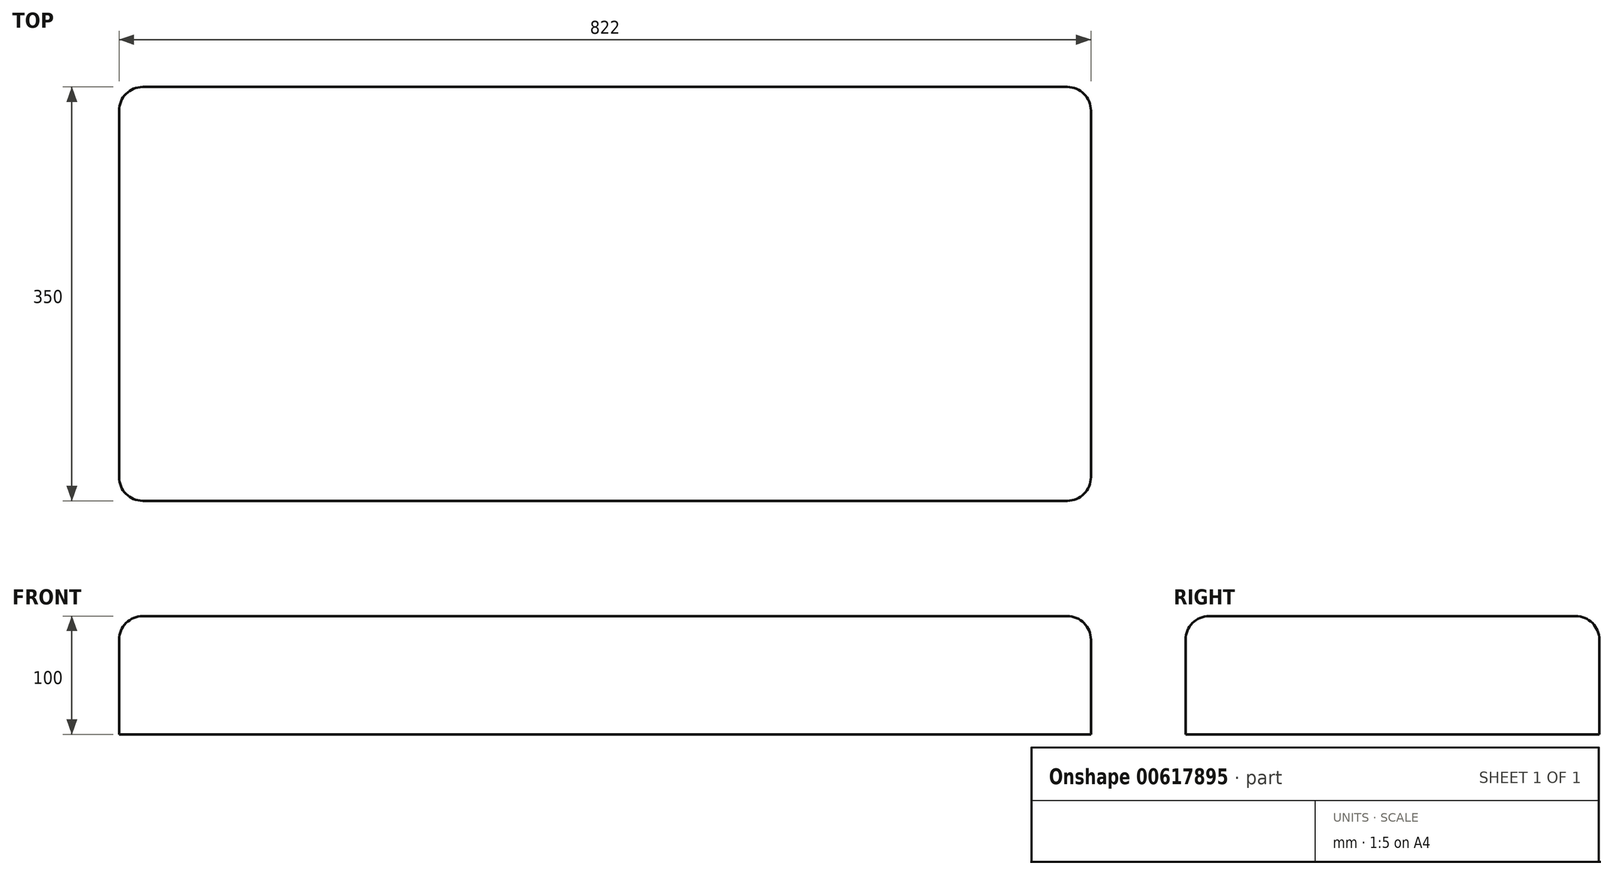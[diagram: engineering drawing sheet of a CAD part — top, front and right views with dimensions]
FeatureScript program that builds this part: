
annotation { "Feature Type Name" : "Feature", "Feature Type Description" : "" }
export const myFeature = defineFeature(function(context is Context, id is Id, definition is map)
    precondition{}
    {
        {
            var Q0;
            Q0=qCreatedBy(makeId("Top.planeOp"),FACE);
            var sketch = newSketch(context, id + "F0", { "sketchPlane" : qUnion([Q0])});
            skLineSegment(sketch, "E0.bottom", {"start": v(411, -175) * mm, "end": v(-411, -175) * mm});
            skLineSegment(sketch, "E0.top", {"start": v(411, 175) * mm, "end": v(-411, 175) * mm});
            skLineSegment(sketch, "E0.left", {"start": v(411, -175) * mm, "end": v(411, 175) * mm});
            skLineSegment(sketch, "E0.right", {"start": v(-411, -175) * mm, "end": v(-411, 175) * mm});
            skPoint(sketch, "E0.middle", {"position": v(0, 0) * mm});
            skSolve(sketch);
        }
        {
            var Q0;
            Q0=qSketchRegion(id+"F0",true);
            extrude(context, id + "F1", {"entities" : qUnion([Q0]), "depth" : 100 * mm, "offsetDistance" : 25 * mm});
        }
        {
            var Q0;
            Q0=makeQuery(id+"F1.opExtrude","CAP_EDGE",EDGE,{"disambiguationData":[OSD([sQuery(id+"F0.wireOp",EDGE,"E0.bottom")])],"isStart":false});
            var Q1;
            Q1=makeQuery(id+"F1.opExtrude","CAP_EDGE",EDGE,{"disambiguationData":[OSD([sQuery(id+"F0.wireOp",EDGE,"E0.right")])],"isStart":false});
            var Q2;
            Q2=makeQuery(id+"F1.opExtrude","CAP_EDGE",EDGE,{"disambiguationData":[OSD([sQuery(id+"F0.wireOp",EDGE,"E0.top")])],"isStart":false});
            var Q3;
            Q3=makeQuery(id+"F1.opExtrude","CAP_EDGE",EDGE,{"disambiguationData":[OSD([sQuery(id+"F0.wireOp",EDGE,"E0.left")])],"isStart":false});
            var Q4;
            Q4=makeQuery(id+"F1.opExtrude","SWEPT_EDGE",EDGE,{"disambiguationData":[OSD([sQuery(id+"F0.wireOp",EDGE,"E0.bottom"),sQuery(id+"F0.wireOp",EDGE,"E0.left")])]});
            var Q5;
            Q5=makeQuery(id+"F1.opExtrude","SWEPT_EDGE",EDGE,{"disambiguationData":[OSD([sQuery(id+"F0.wireOp",EDGE,"E0.top"),sQuery(id+"F0.wireOp",EDGE,"E0.left")])]});
            var Q6;
            Q6=makeQuery(id+"F1.opExtrude","SWEPT_EDGE",EDGE,{"disambiguationData":[OSD([sQuery(id+"F0.wireOp",EDGE,"E0.bottom"),sQuery(id+"F0.wireOp",EDGE,"E0.right")])]});
            var Q7;
            Q7=makeQuery(id+"F1.opExtrude","SWEPT_EDGE",EDGE,{"disambiguationData":[OSD([sQuery(id+"F0.wireOp",EDGE,"E0.top"),sQuery(id+"F0.wireOp",EDGE,"E0.right")])]});
            fillet(context, id + "F2", {"entities" : qUnion([Q0, Q1, Q2, Q3, Q4, Q5, Q6, Q7]), "radius" : 20 * mm, "tangentPropagation" : true, "allowEdgeOverflow" : false});
        }
    });
